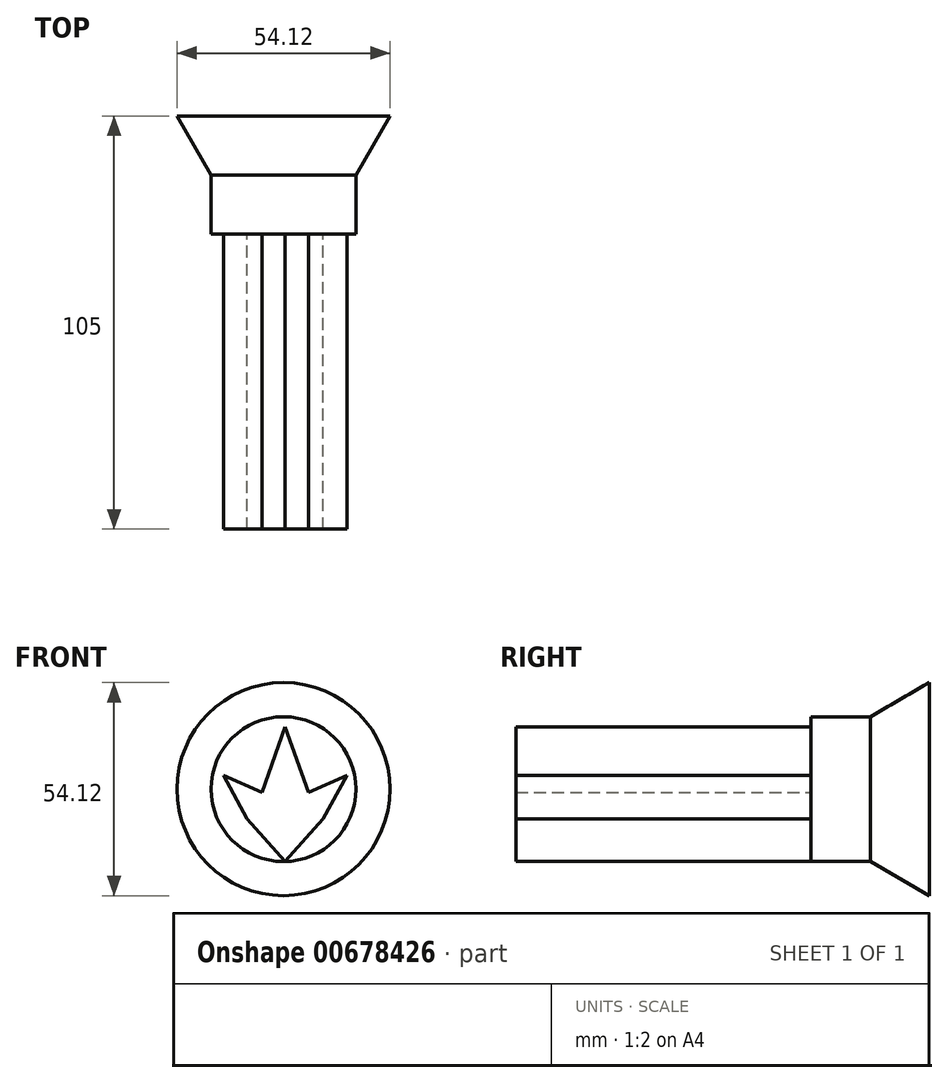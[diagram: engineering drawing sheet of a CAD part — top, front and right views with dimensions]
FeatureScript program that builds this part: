
annotation { "Feature Type Name" : "Feature", "Feature Type Description" : "" }
export const myFeature = defineFeature(function(context is Context, id is Id, definition is map)
    precondition{}
    {
        {
            var Q0;
            Q0=qCreatedBy(makeId("Front.planeOp"),FACE);
            var sketch = newSketch(context, id + "F0", { "sketchPlane" : qUnion([Q0])});
            skLineSegment(sketch, "E0", {"start": v(-9.2, -7.62) * mm, "end": v(-15.23, 3.45) * mm});
            skLineSegment(sketch, "E1", {"start": v(-15.23, 3.45) * mm, "end": v(-5.46, -0.86) * mm});
            skLineSegment(sketch, "E2", {"start": v(-5.46, -0.86) * mm, "end": v(0.43, 15.8) * mm});
            skLineSegment(sketch, "E3", {"start": v(-9.2, -7.62) * mm, "end": v(0.43, -18.4) * mm});
            skLineSegment(sketch, "E4.MirrorCS", {"start": v(6.32, -0.86) * mm, "end": v(0.43, 15.8) * mm});
            skLineSegment(sketch, "E5.MirrorCS", {"start": v(16.1, 3.45) * mm, "end": v(6.32, -0.86) * mm});
            skLineSegment(sketch, "E6.MirrorCS", {"start": v(10.06, -7.62) * mm, "end": v(16.1, 3.45) * mm});
            skLineSegment(sketch, "E7.MirrorCS", {"start": v(10.06, -7.62) * mm, "end": v(0.43, -18.4) * mm});
            skSolve(sketch);
        }
        {
            var Q0;
            Q0=makeQuery(id+"F0.imprint","IMPRINT",FACE,{"disambiguationData":[TD([[makeQuery(id+"F0.imprint","IMPRINT",EDGE,{"derivedFrom":sQuery(id+"F0.wireOp",EDGE,"E0")}),-1.0]])]});
            extrude(context, id + "F1", {"entities" : qUnion([Q0]), "depth" : 75 * mm, "offsetDistance" : 25 * mm});
        }
        {
            var Q0;
            Q0=makeQuery(id+"F1.opExtrude","CAP_FACE",FACE,{"disambiguationData":[OSD([sQuery(id+"F0.wireOp",EDGE,"E0"),sQuery(id+"F0.wireOp",EDGE,"E1"),sQuery(id+"F0.wireOp",EDGE,"E2"),sQuery(id+"F0.wireOp",EDGE,"E3"),sQuery(id+"F0.wireOp",EDGE,"E4.MirrorCS"),sQuery(id+"F0.wireOp",EDGE,"E5.MirrorCS"),sQuery(id+"F0.wireOp",EDGE,"E6.MirrorCS"),sQuery(id+"F0.wireOp",EDGE,"E7.MirrorCS")])],"isStart":true});
            var sketch = newSketch(context, id + "F2", { "sketchPlane" : qUnion([Q0])});
            skCircle(sketch, "E8", {"center": v(0, 0) * mm, "radius": 18.4 * mm});
            skSolve(sketch);
        }
        {
            var Q0;
            Q0=makeQuery(id+"F2.imprint","IMPRINT",FACE,{"disambiguationData":[TD([[makeQuery(id+"F2.imprint","IMPRINT",EDGE,{"derivedFrom":makeQuery(id+"F1.opExtrude","CAP_EDGE",EDGE,{"disambiguationData":[OSD([sQuery(id+"F0.wireOp",EDGE,"E0")])],"isStart":true})}),1.0]])]});
            var Q1;
            Q1=makeQuery(id+"F2.imprint","IMPRINT",FACE,{"disambiguationData":[TD([[makeQuery(id+"F2.imprint","IMPRINT",EDGE,{"derivedFrom":sQuery(id+"F2.wireOp",EDGE,"E8")}),1.0]])]});
            extrude(context, id + "F3", {"entities" : qUnion([Q0, Q1]), "operationType" : NewBodyOperationType.ADD, "depth" : 15 * mm, "offsetDistance" : 25 * mm});
        }
        {
            var Q0;
            Q0=makeQuery(id+"F3.opExtrude","CAP_FACE",FACE,{"disambiguationData":[OSD([sQuery(id+"F2.wireOp",EDGE,"E8")])],"isStart":false});
            extrude(context, id + "F4", {"entities" : qUnion([Q0]), "operationType" : NewBodyOperationType.ADD, "depth" : 15 * mm, "offsetDistance" : 25 * mm, "hasDraft" : true, "draftAngle" : 30 * degree});
        }
    });
